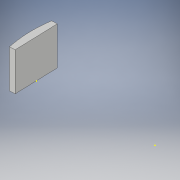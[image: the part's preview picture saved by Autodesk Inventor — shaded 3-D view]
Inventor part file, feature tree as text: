
AUTODESK INVENTOR PART (.ipt)
format: ipt  version: 2019 (Build 230136000, 136)  size: 105,984 bytes
history: native  units: in
note: dims shown in document units (in); Inventor stores cm internally (conversion verified against a paired STEP export)
features: sketch x7, extrude x2, split x1, plane x1
ambient origin geometry x8: Origin, YZ Plane, XZ Plane, XY Plane, X Axis, Y Axis, Z Axis, Center Point
bodies: Solid1 (feature_tree)
feature tree (11):
  sketch  "Sketch1"  dims[d0=17.7165in d1=2.7559in d2=0.0in]
  extrude  "Extrusion1"  Depth=2.7559in TaperAngle=0.0deg
  split  "Split1"
  sketch  "3D Sketch1"
  extrude  "Extrusion2"  Depth=0.3937in TaperAngle=0.0deg
  sketch  "Sketch5"
  sketch  "3D Sketch2"
  plane  "Work Plane1"
  sketch  "Sketch2"  dims[d3=3.1496in d4=0.3937in d5=0.0in]
  sketch  "Sketch3"
  sketch  "Sketch4"
